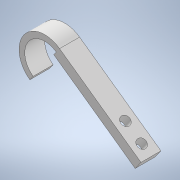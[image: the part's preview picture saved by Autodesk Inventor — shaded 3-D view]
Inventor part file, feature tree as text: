
AUTODESK INVENTOR PART (.ipt)
format: ipt  version: 2020 (Build 240168000, 168)  size: 175,616 bytes
history: native  units: mm
features: sketch x4, extrude x4, projected_geometry x3, other x3, reference x2, plane x1, thicken_offset x1, chamfer x1
ambient origin geometry x8: Origin, YZ Plane, XZ Plane, XY Plane, X Axis, Y Axis, Z Axis, Center Point
bodies: Solid1 (feature_tree)
feature tree (19):
  sketch  "Sketch1"  dims[d0=3.0mm d1=3.5mm]
  plane  "Work Plane1"
  extrude  "Extrusion1"  Depth=3.5mm
  extrude  "Extrusion3"  Depth=18.0mm
  thicken_offset  "Thicken1"
  extrude  "Extrusion4"  Depth=14.0mm
  extrude  "Extrusion5"  Depth=10.0mm
  chamfer  "Chamfer2"  Distance=10.0mm
  reference  "Reference1"
  reference  "Reference2"
  sketch  "Sketch3"  dims[d2=35.0mm d5=18.0mm]
  projected_geometry  "Projected Loop1"
  sketch  "Sketch4"  dims[d6=2.0mm d7=14.0mm]
  projected_geometry  "Projected Loop2"
  sketch  "Sketch5"  dims[d8=10.0mm d9=0.0mm d17=15.0mm d18=10.0mm d19=0.0mm d20=12.0mm d21=12.0mm d22=30.0mm d23=18.849556mm d24=3.5mm d25=10.0mm d26=0.0mm d27=6.981317mm d28=10.0mm d29=0.0mm d30=1.5mm d31=2.0mm d32=60.0deg]
  projected_geometry  "Projected Loop3"
  parser-record x1  (decoder bookkeeping rows leaked as tree rows — omitted from the tree; the rows remain in map.json)
  other  "leg_1.iam"
  other  "leg_link_1:1"
note: 1 file-system path scrubbed to <path> (originals preserved in map.json)
